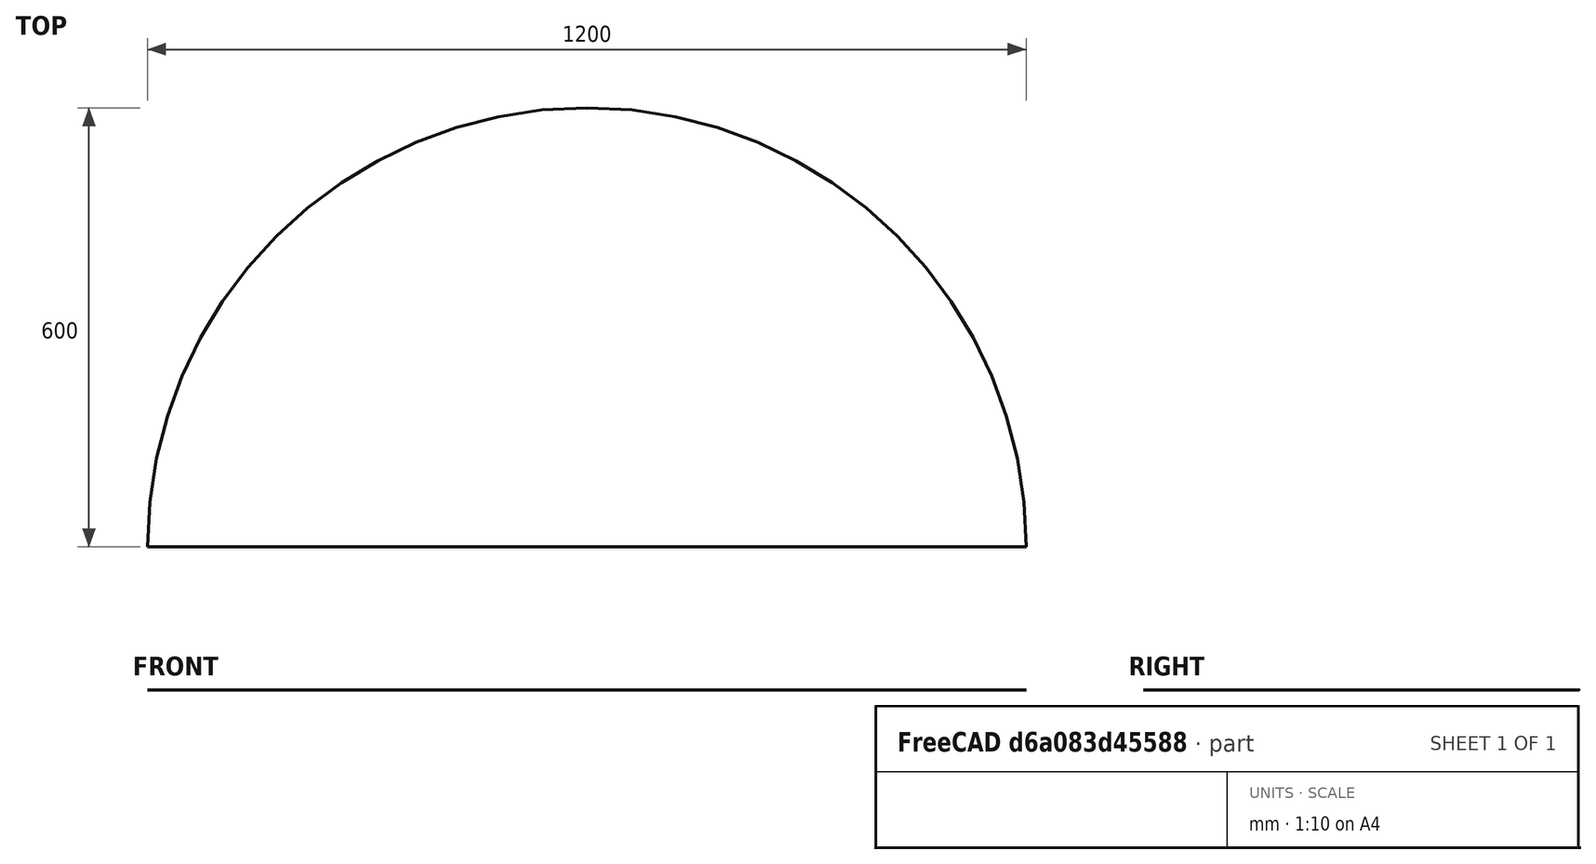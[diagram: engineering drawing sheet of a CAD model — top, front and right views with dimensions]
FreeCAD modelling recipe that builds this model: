
FCSTD DOCUMENT  (FreeCAD 0.21R33668 +26 (Git))
Label: agrawal1981
License: All rights reserved
LicenseURL: http://en.wikipedia.org/wiki/All_rights_reserved
objects: Part::Part2DObjectPython×9, App::DocumentObjectGroup×3, Spreadsheet::Sheet×1, Part::Cut×1
note: 10 computed .brp shape members not serialized (recipe doc carries the construction recipe); baked Part::Feature solids carry a one-line shape summary decoded from their .brp

FEATURE [Part::Part2DObjectPython] Circle001  label="Conductor_001"  # Draft 2D object (typed FeaturePython)
  Area = 14.4721
  FirstAngle = 0
  LastAngle = 0
  MakeFace = true
  Placement = pos=(0,84.527,0) rot=(0,0,1;0rad)
  Radius = 2.1463
  expr: .Placement.Base.y = Spreadsheet.w1_extra_height
  expr: Radius = Spreadsheet.r_wire
FEATURE [Part::Part2DObjectPython] Circle002  label="Dielectric_001"  # Draft 2D object (typed FeaturePython)
  Area = 29.1864
  FirstAngle = 0
  LastAngle = 0
  MakeFace = true
  Placement = pos=(0,84.527,0) rot=(0,0,1;0rad)
  Radius = 3.048
  expr: .Placement.Base.y = Spreadsheet.w1_extra_height
  expr: Radius = Spreadsheet.r_dielectric
FEATURE [App::DocumentObjectGroup] Group  label="solid_wire_001"
  Group = -> [Circle001,Circle002]
FEATURE [Spreadsheet::Sheet] Spreadsheet
  cells = A2='Wire radius; B2(r_wire)==0.42926 cm / 2; A3='Dielectric radius; B3(r_dielectric)==0.6096 cm / 2; A4='Center wire (w1) height; B4(w1_extra_height)==84.527 mm; A5='Side wires (w3, w2) height; B5(side_wires_height)==79.248 mm; A6='Side wires horizontal distance; B6(side_wires_horizontal_distance)==3.048 mm; A7='Outer domain radius; B7(rd)==600 mm; A8='Dielectric permittivity; B8(eps_r)=2.26
FEATURE [Part::Part2DObjectPython] Circle005  label="Conductor_003"  # Draft 2D object (typed FeaturePython)
  Area = 14.4721
  FirstAngle = 0
  LastAngle = 0
  MakeFace = true
  Placement = pos=(3.048,79.248,0) rot=(0,0,1;0rad)
  Radius = 2.1463
  expr: .Placement.Base.x = Spreadsheet.side_wires_horizontal_distance
  expr: .Placement.Base.y = Spreadsheet.side_wires_height
  expr: Radius = Spreadsheet.r_wire
FEATURE [Part::Part2DObjectPython] Circle006  label="Dielectric_003"  # Draft 2D object (typed FeaturePython)
  Area = 29.1864
  FirstAngle = 0
  LastAngle = 0
  MakeFace = true
  Placement = pos=(3.048,79.248,0) rot=(0,0,1;0rad)
  Radius = 3.048
  expr: .Placement.Base.x = Spreadsheet.side_wires_horizontal_distance
  expr: .Placement.Base.y = Spreadsheet.side_wires_height
  expr: Radius = Spreadsheet.r_dielectric
FEATURE [App::DocumentObjectGroup] Group002  label="solid_wire_003"
  Group = -> [Circle005,Circle006]
FEATURE [Part::Part2DObjectPython] Circle  # Draft 2D object (typed FeaturePython)
  Area = 1.13097e+06
  FirstAngle = 0
  LastAngle = 0
  MakeFace = true
  Radius = 600
  expr: Radius = Spreadsheet.rd
FEATURE [Part::Part2DObjectPython] Rectangle  # Draft 2D object (typed FeaturePython)
  Area = 720000
  ChamferSize = 0
  Columns = 1
  FilletRadius = 0
  Height = -600
  Length = 1200
  MakeFace = true
  Placement = pos=(-600,0,0) rot=(0,0,1;0rad)
  Rows = 1
  expr: .Placement.Base.x = -Spreadsheet.rd
  expr: .Placement.Base.y = 0
  expr: Height = -Spreadsheet.rd
  expr: Length = Spreadsheet.rd * 2
FEATURE [Part::Cut] Cut  label="OpenBoundary_0"
  Base = -> Circle
  Tool = -> Rectangle
FEATURE [Part::Part2DObjectPython] Circle004  label="Dielectric_002"  # Draft 2D object (typed FeaturePython)
  Area = 29.1864
  FirstAngle = 0
  LastAngle = 0
  MakeFace = true
  Placement = pos=(-3.048,79.248,0) rot=(0,0,1;0rad)
  Radius = 3.048
  expr: .Placement.Base.x = -Spreadsheet.side_wires_horizontal_distance
  expr: .Placement.Base.y = Spreadsheet.side_wires_height
  expr: Radius = Spreadsheet.r_dielectric
FEATURE [Part::Part2DObjectPython] Circle003  label="Conductor_002"  # Draft 2D object (typed FeaturePython)
  Area = 14.4721
  FirstAngle = 0
  LastAngle = 0
  MakeFace = true
  Placement = pos=(-3.048,79.25,0) rot=(0,0,1;0rad)
  Radius = 2.1463
  expr: .Placement.Base.x = -Spreadsheet.side_wires_horizontal_distance
  expr: Radius = Spreadsheet.r_wire
FEATURE [App::DocumentObjectGroup] Group001  label="solid_wire_002"
  Group = -> [Circle003,Circle004]
FEATURE [Part::Part2DObjectPython] Rectangle001  label="Conductor_0"  # Draft 2D object (typed FeaturePython)
  Area = 720000
  ChamferSize = 0
  Columns = 1
  FilletRadius = 0
  Height = -600
  Length = 1200
  MakeFace = true
  Placement = pos=(-600,0,0) rot=(0,0,1;0rad)
  Rows = 1
  expr: .Placement.Base.x = -Spreadsheet.rd
  expr: .Placement.Base.y = 0
  expr: Height = -Spreadsheet.rd
  expr: Length = Spreadsheet.rd * 2
